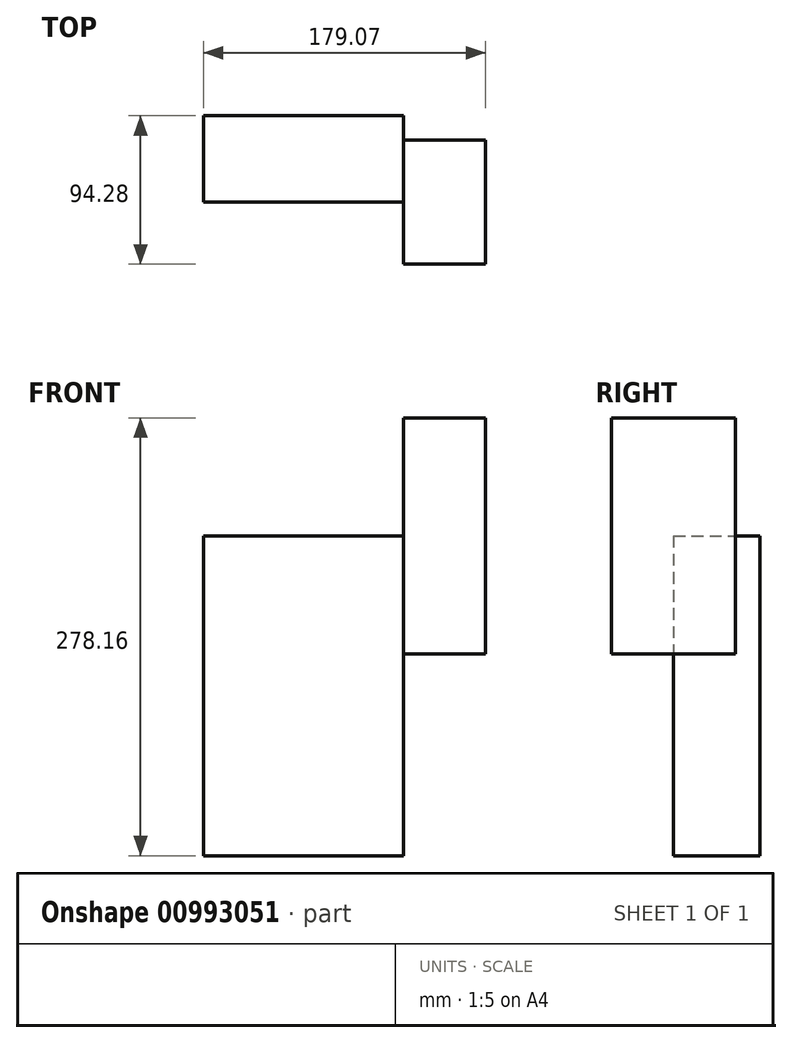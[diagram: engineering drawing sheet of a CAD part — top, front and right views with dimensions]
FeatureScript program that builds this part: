
annotation { "Feature Type Name" : "Feature", "Feature Type Description" : "" }
export const myFeature = defineFeature(function(context is Context, id is Id, definition is map)
    precondition{}
    {
        {
            var Q0;
            Q0=qCreatedBy(makeId("Front.planeOp"),FACE);
            var sketch = newSketch(context, id + "F0", { "sketchPlane" : qUnion([Q0])});
            skLineSegment(sketch, "E0.bottom", {"start": v(63.5, 101.6) * mm, "end": v(-63.5, 101.6) * mm});
            skLineSegment(sketch, "E0.top", {"start": v(63.5, -101.6) * mm, "end": v(-63.5, -101.6) * mm});
            skLineSegment(sketch, "E0.left", {"start": v(63.5, 101.6) * mm, "end": v(63.5, -101.6) * mm});
            skLineSegment(sketch, "E0.right", {"start": v(-63.5, 101.6) * mm, "end": v(-63.5, -101.6) * mm});
            skPoint(sketch, "E0.middle", {"position": v(0, 0) * mm});
            skSolve(sketch);
        }
        {
            var Q0;
            Q0=makeQuery(id+"F0.imprint","IMPRINT",FACE,{"disambiguationData":[TD([[makeQuery(id+"F0.imprint","IMPRINT",EDGE,{"derivedFrom":sQuery(id+"F0.wireOp",EDGE,"E0.bottom")}),1.0]])]});
            extrude(context, id + "F1", {"entities" : qUnion([Q0]), "depth" : 54.86 * mm, "offsetDistance" : 25.4 * mm});
        }
        {
            var Q0;
            Q0=makeQuery(id+"F1.opExtrude","SWEPT_FACE",FACE,{"disambiguationData":[OSD([sQuery(id+"F0.wireOp",EDGE,"E0.left")])]});
            var sketch = newSketch(context, id + "F2", { "sketchPlane" : qUnion([Q0])});
            skLineSegment(sketch, "E1.bottom", {"start": v(-94.28, 176.56) * mm, "end": v(-15.45, 176.56) * mm});
            skLineSegment(sketch, "E1.top", {"start": v(-94.28, 26.64) * mm, "end": v(-15.45, 26.64) * mm});
            skLineSegment(sketch, "E1.left", {"start": v(-94.28, 176.56) * mm, "end": v(-94.28, 26.64) * mm});
            skLineSegment(sketch, "E1.right", {"start": v(-15.45, 176.56) * mm, "end": v(-15.45, 26.64) * mm});
            skPoint(sketch, "E1.middle", {"position": v(-54.86, 101.6) * mm});
            skSolve(sketch);
        }
        {
            var Q0;
            {var subQ1=sQuery(id+"F2.wireOp",EDGE,"E1.bottom");Q0=makeQuery(id+"F2.imprint","IMPRINT",FACE,{"disambiguationData":[TD([[makeQuery(id+"F2.imprint","IMPRINT",EDGE,{"derivedFrom":subQ1}),-1.0]])]});}
            var Q1;
            {var subQ0=sQuery(id+"F2.wireOp",EDGE,"E1.right");var subQ1=sQuery(id+"F2.wireOp",EDGE,"E1.top");var subQ2=makeQuery(id+"F2.imprint","INTERSECT",VERTEX,{"derivedFrom":[subQ1,subQ0]});Q1=makeQuery(id+"F2.imprint","IMPRINT",FACE,{"disambiguationData":[TD([[makeQuery(id+"F2.imprint","IMPRINT",EDGE,{"disambiguationData":[TD([[subQ2,1.0]])],"derivedFrom":subQ1}),1.0]])]});}
            extrude(context, id + "F3", {"entities" : qUnion([Q0, Q1]), "depth" : 52.07 * mm, "offsetDistance" : 25.4 * mm});
        }
    });
